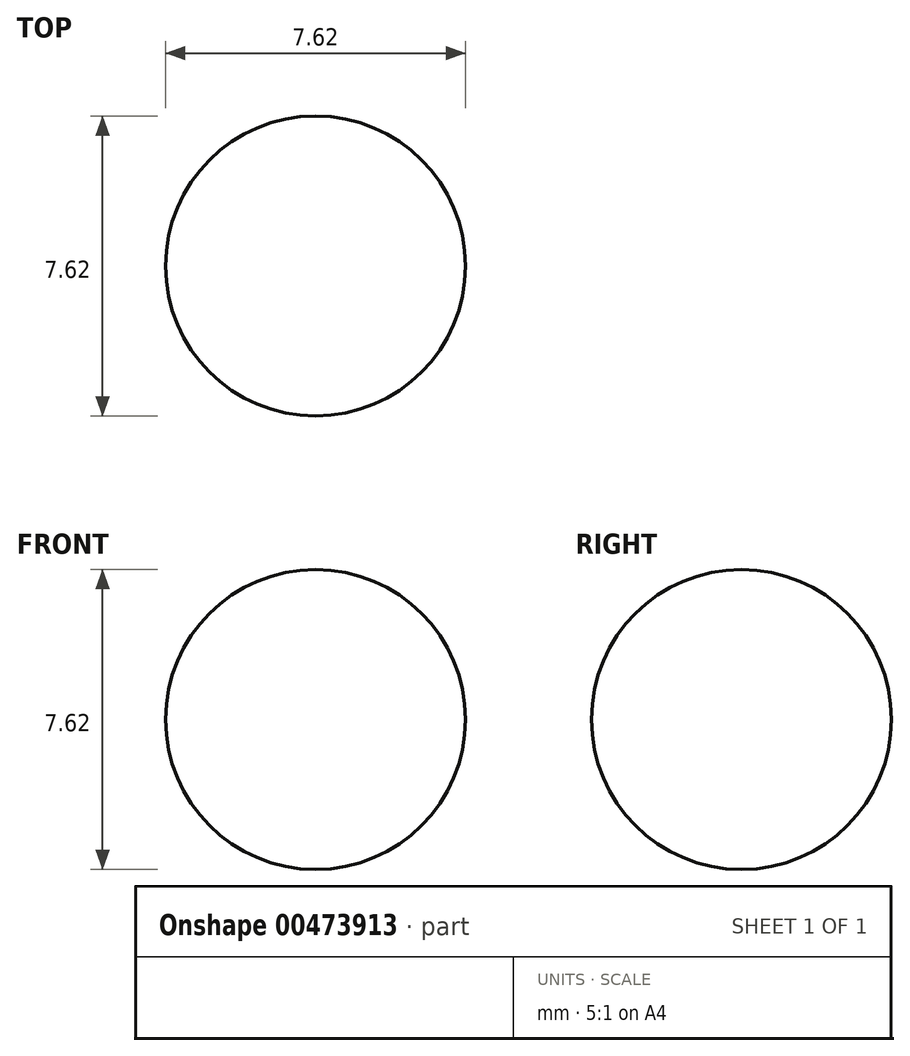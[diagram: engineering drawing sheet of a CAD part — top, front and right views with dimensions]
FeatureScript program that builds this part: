
annotation { "Feature Type Name" : "Feature", "Feature Type Description" : "" }
export const myFeature = defineFeature(function(context is Context, id is Id, definition is map)
    precondition{}
    {
        {
            var Q0;
            Q0=qCreatedBy(makeId("Front.planeOp"),FACE);
            var sketch = newSketch(context, id + "F0", { "sketchPlane" : qUnion([Q0])});
            skLineSegment(sketch, "E0", {"start": v(0, 0) * mm, "end": v(0, 7.62) * mm});
            skArc(sketch, "E1", {"start": v(0, 0) * mm, "mid": v(3.81, 3.8) * mm, "end": v(0, 7.62) * mm});
            skSolve(sketch);
        }
        {
            var Q0;
            Q0=makeQuery(id+"F0.imprint","IMPRINT",FACE,{"disambiguationData":[TD([[makeQuery(id+"F0.imprint","IMPRINT",EDGE,{"derivedFrom":sQuery(id+"F0.wireOp",EDGE,"E0")}),-1.0]])]});
            var Q1;
            Q1=sQuery(id+"F0.wireOp",EDGE,"E0");
            revolve(context, id + "F1", {"entities" : qUnion([Q0]), "axis" : qUnion([Q1]), "revolveType" : RevolveType.FULL});
        }
    });
